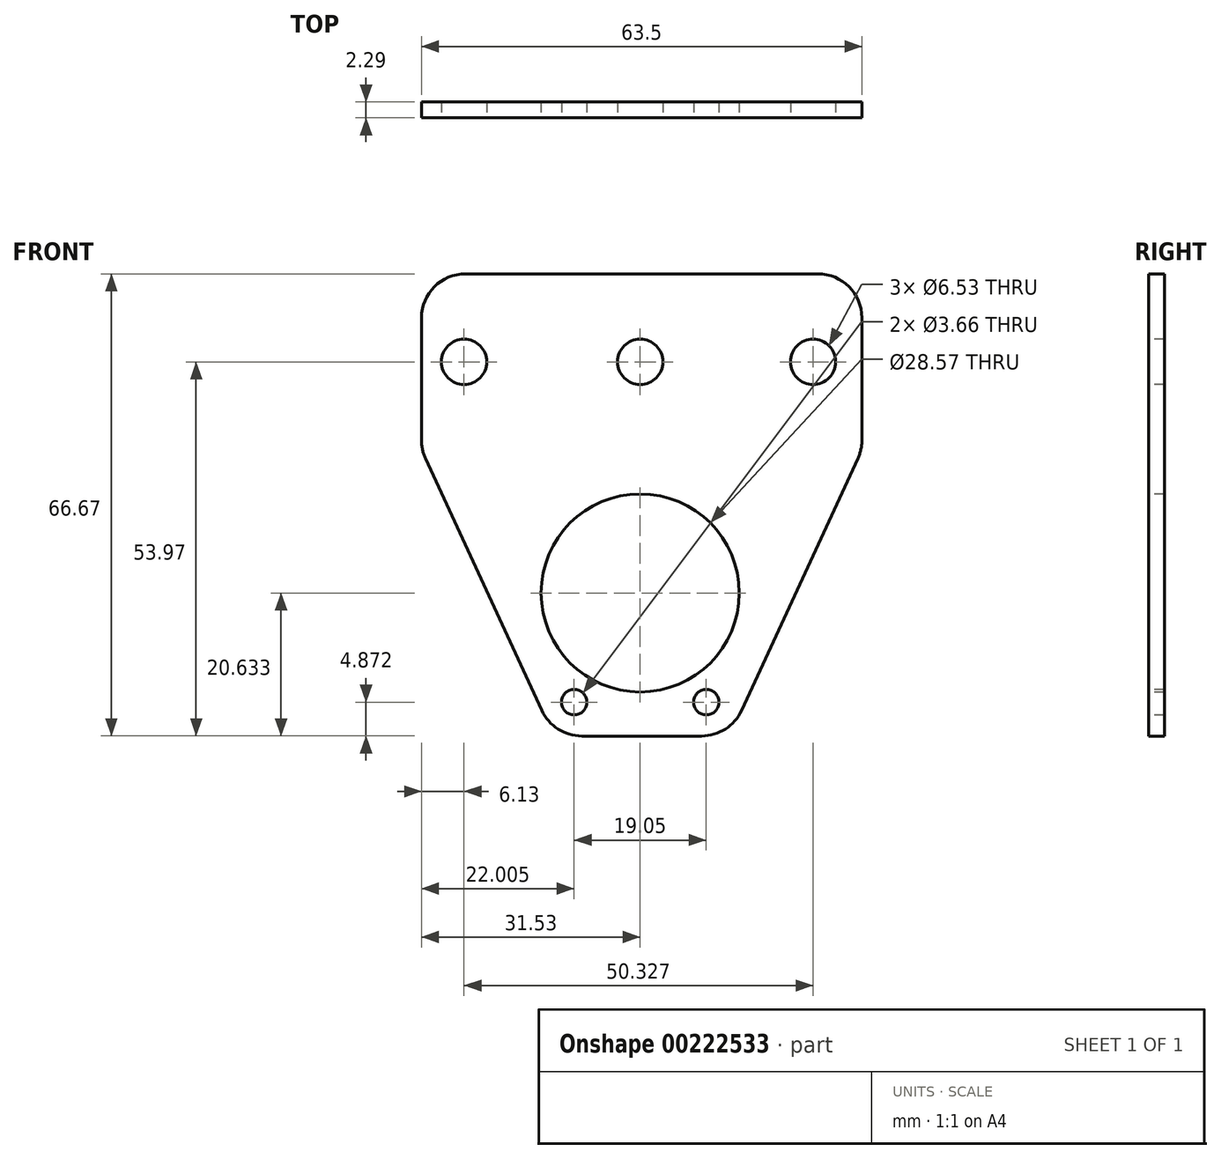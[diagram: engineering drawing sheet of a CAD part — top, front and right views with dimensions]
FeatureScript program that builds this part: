
annotation { "Feature Type Name" : "Feature", "Feature Type Description" : "" }
export const myFeature = defineFeature(function(context is Context, id is Id, definition is map)
    precondition{}
    {
        {
            var Q0;
            Q0=qCreatedBy(makeId("Front.planeOp"),FACE);
            var sketch = newSketch(context, id + "F0", { "sketchPlane" : qUnion([Q0])});
            skLineSegment(sketch, "E0", {"start": v(-25.18, 42.8) * mm, "end": v(25.62, 42.8) * mm});
            skLineSegment(sketch, "E1", {"start": v(31.97, 36.44) * mm, "end": v(31.97, 18.78) * mm});
            skLineSegment(sketch, "E2", {"start": v(31.38, 16.12) * mm, "end": v(14.62, -20.2) * mm});
            skLineSegment(sketch, "E3", {"start": v(8.85, -23.88) * mm, "end": v(-8.42, -23.88) * mm});
            skLineSegment(sketch, "E4", {"start": v(-14.19, -20.2) * mm, "end": v(-30.95, 16.12) * mm});
            skLineSegment(sketch, "E5", {"start": v(-31.53, 18.78) * mm, "end": v(-31.53, 36.44) * mm});
            skPoint(sketch, "E6.visualSharp", {"position": v(-31.53, 42.8) * mm});
            skArc(sketch, "E6.filletArc", {"start": v(-25.18, 42.8) * mm, "mid": v(-29.67, 40.93) * mm, "end": v(-31.53, 36.44) * mm});
            skPoint(sketch, "E7.visualSharp", {"position": v(31.97, 42.8) * mm});
            skArc(sketch, "E7.filletArc", {"start": v(31.97, 36.44) * mm, "mid": v(30.1, 40.93) * mm, "end": v(25.62, 42.8) * mm});
            skPoint(sketch, "E8.visualSharp", {"position": v(31.97, 17.4) * mm});
            skArc(sketch, "E8.filletArc", {"start": v(31.38, 16.12) * mm, "mid": v(31.82, 17.42) * mm, "end": v(31.97, 18.78) * mm});
            skPoint(sketch, "E9.visualSharp", {"position": v(-31.53, 17.4) * mm});
            skArc(sketch, "E9.filletArc", {"start": v(-31.53, 18.78) * mm, "mid": v(-31.39, 17.42) * mm, "end": v(-30.95, 16.12) * mm});
            skPoint(sketch, "E10.visualSharp", {"position": v(-12.48, -23.88) * mm});
            skArc(sketch, "E10.filletArc", {"start": v(-14.19, -20.2) * mm, "mid": v(-11.84, -22.88) * mm, "end": v(-8.42, -23.88) * mm});
            skPoint(sketch, "E11.visualSharp", {"position": v(12.92, -23.88) * mm});
            skArc(sketch, "E11.filletArc", {"start": v(8.85, -23.88) * mm, "mid": v(12.28, -22.88) * mm, "end": v(14.62, -20.2) * mm});
            skSolve(sketch);
        }
        {
            var Q0;
            Q0=makeQuery(id+"F0.imprint","IMPRINT",FACE,{"disambiguationData":[TD([[makeQuery(id+"F0.imprint","IMPRINT",EDGE,{"derivedFrom":sQuery(id+"F0.wireOp",EDGE,"E0")}),-1.0]])]});
            extrude(context, id + "F1", {"entities" : qUnion([Q0]), "depth" : 2.3 * mm});
        }
        {
            var Q0;
            Q0=makeQuery(id+"F1.opExtrude","CAP_FACE",FACE,{"disambiguationData":[OSD([sQuery(id+"F0.wireOp",EDGE,"E0"),sQuery(id+"F0.wireOp",EDGE,"E1"),sQuery(id+"F0.wireOp",EDGE,"E2"),sQuery(id+"F0.wireOp",EDGE,"E3"),sQuery(id+"F0.wireOp",EDGE,"E4"),sQuery(id+"F0.wireOp",EDGE,"E5"),sQuery(id+"F0.wireOp",EDGE,"E6.filletArc"),sQuery(id+"F0.wireOp",EDGE,"E7.filletArc"),sQuery(id+"F0.wireOp",EDGE,"E8.filletArc"),sQuery(id+"F0.wireOp",EDGE,"E9.filletArc"),sQuery(id+"F0.wireOp",EDGE,"E10.filletArc"),sQuery(id+"F0.wireOp",EDGE,"E11.filletArc")])],"isStart":false});
            var sketch = newSketch(context, id + "F2", { "sketchPlane" : qUnion([Q0])});
            skPoint(sketch, "E12", {"position": v(-25.4, 30.1) * mm});
            skPoint(sketch, "E13", {"position": v(0, 30.1) * mm});
            skPoint(sketch, "E14", {"position": v(24.93, 30.1) * mm});
            skSolve(sketch);
        }
        {
            var Q0;
            Q0=sQuery(id+"F2.wireOp",VERTEX,"E12");
            var Q1;
            Q1=sQuery(id+"F2.wireOp",VERTEX,"E13");
            var Q2;
            Q2=sQuery(id+"F2.wireOp",VERTEX,"E14");
            var Q3;
            Q3=makeQuery(id+"F1.opExtrude","SWEPT_BODY",BODY,{"disambiguationData":[OSD([sQuery(id+"F0.wireOp",EDGE,"E0"),sQuery(id+"F0.wireOp",EDGE,"E1"),sQuery(id+"F0.wireOp",EDGE,"E2"),sQuery(id+"F0.wireOp",EDGE,"E3"),sQuery(id+"F0.wireOp",EDGE,"E4"),sQuery(id+"F0.wireOp",EDGE,"E5"),sQuery(id+"F0.wireOp",EDGE,"E6.filletArc"),sQuery(id+"F0.wireOp",EDGE,"E7.filletArc"),sQuery(id+"F0.wireOp",EDGE,"E8.filletArc"),sQuery(id+"F0.wireOp",EDGE,"E9.filletArc"),sQuery(id+"F0.wireOp",EDGE,"E10.filletArc"),sQuery(id+"F0.wireOp",EDGE,"E11.filletArc")])]});
            hole(context, id + "F3", {"style" : HoleStyle.SIMPLE, "endStyle" : HoleEndStyle.THROUGH, "standardTappedOrClearance" : lookupTablePath({ "standard" : "ANSI", "fit" : "Close", "size" : "1/4", "type" : "Clearance" }), "standardBlindInLast" : lookupTablePath({ "fit" : "Close", "standard" : "ANSI", "size" : "1/4", "type" : "Clearance" }), "holeDiameter" : 6.53 * mm, "locations" : qUnion([Q0, Q1, Q2]), "scope" : qUnion([Q3]), "isTappedThrough" : true});
        }
        {
            var Q0;
            Q0=makeQuery(id+"F1.opExtrude","CAP_FACE",FACE,{"disambiguationData":[OSD([sQuery(id+"F0.wireOp",EDGE,"E0"),sQuery(id+"F0.wireOp",EDGE,"E1"),sQuery(id+"F0.wireOp",EDGE,"E2"),sQuery(id+"F0.wireOp",EDGE,"E3"),sQuery(id+"F0.wireOp",EDGE,"E4"),sQuery(id+"F0.wireOp",EDGE,"E5"),sQuery(id+"F0.wireOp",EDGE,"E6.filletArc"),sQuery(id+"F0.wireOp",EDGE,"E7.filletArc"),sQuery(id+"F0.wireOp",EDGE,"E8.filletArc"),sQuery(id+"F0.wireOp",EDGE,"E9.filletArc"),sQuery(id+"F0.wireOp",EDGE,"E10.filletArc"),sQuery(id+"F0.wireOp",EDGE,"E11.filletArc")])],"isStart":false});
            var sketch = newSketch(context, id + "F4", { "sketchPlane" : qUnion([Q0])});
            skPoint(sketch, "E15", {"position": v(0, -3.25) * mm});
            skSolve(sketch);
        }
        {
            var Q0;
            Q0=sQuery(id+"F4.wireOp",VERTEX,"E15");
            var Q1;
            Q1=makeQuery(id+"F1.opExtrude","SWEPT_BODY",BODY,{"disambiguationData":[OSD([sQuery(id+"F0.wireOp",EDGE,"E0"),sQuery(id+"F0.wireOp",EDGE,"E1"),sQuery(id+"F0.wireOp",EDGE,"E2"),sQuery(id+"F0.wireOp",EDGE,"E3"),sQuery(id+"F0.wireOp",EDGE,"E4"),sQuery(id+"F0.wireOp",EDGE,"E5"),sQuery(id+"F0.wireOp",EDGE,"E6.filletArc"),sQuery(id+"F0.wireOp",EDGE,"E7.filletArc"),sQuery(id+"F0.wireOp",EDGE,"E8.filletArc"),sQuery(id+"F0.wireOp",EDGE,"E9.filletArc"),sQuery(id+"F0.wireOp",EDGE,"E10.filletArc"),sQuery(id+"F0.wireOp",EDGE,"E11.filletArc")])]});
            hole(context, id + "F5", {"style" : HoleStyle.SIMPLE, "endStyle" : HoleEndStyle.THROUGH, "holeDiameter" : 28.57 * mm, "locations" : qUnion([Q0]), "scope" : qUnion([Q1]), "isTappedThrough" : true});
        }
        {
            var Q0;
            Q0=makeQuery(id+"F1.opExtrude","CAP_FACE",FACE,{"disambiguationData":[OSD([sQuery(id+"F0.wireOp",EDGE,"E0"),sQuery(id+"F0.wireOp",EDGE,"E1"),sQuery(id+"F0.wireOp",EDGE,"E2"),sQuery(id+"F0.wireOp",EDGE,"E3"),sQuery(id+"F0.wireOp",EDGE,"E4"),sQuery(id+"F0.wireOp",EDGE,"E5"),sQuery(id+"F0.wireOp",EDGE,"E6.filletArc"),sQuery(id+"F0.wireOp",EDGE,"E7.filletArc"),sQuery(id+"F0.wireOp",EDGE,"E8.filletArc"),sQuery(id+"F0.wireOp",EDGE,"E9.filletArc"),sQuery(id+"F0.wireOp",EDGE,"E10.filletArc"),sQuery(id+"F0.wireOp",EDGE,"E11.filletArc")])],"isStart":false});
            var sketch = newSketch(context, id + "F6", { "sketchPlane" : qUnion([Q0])});
            skPoint(sketch, "E16", {"position": v(-9.52, -19) * mm});
            skPoint(sketch, "E17", {"position": v(9.53, -19) * mm});
            skSolve(sketch);
        }
        {
            var Q0;
            Q0=sQuery(id+"F6.wireOp",VERTEX,"E16");
            var Q1;
            Q1=sQuery(id+"F6.wireOp",VERTEX,"E17");
            var Q2;
            Q2=makeQuery(id+"F1.opExtrude","SWEPT_BODY",BODY,{"disambiguationData":[OSD([sQuery(id+"F0.wireOp",EDGE,"E0"),sQuery(id+"F0.wireOp",EDGE,"E1"),sQuery(id+"F0.wireOp",EDGE,"E2"),sQuery(id+"F0.wireOp",EDGE,"E3"),sQuery(id+"F0.wireOp",EDGE,"E4"),sQuery(id+"F0.wireOp",EDGE,"E5"),sQuery(id+"F0.wireOp",EDGE,"E6.filletArc"),sQuery(id+"F0.wireOp",EDGE,"E7.filletArc"),sQuery(id+"F0.wireOp",EDGE,"E8.filletArc"),sQuery(id+"F0.wireOp",EDGE,"E9.filletArc"),sQuery(id+"F0.wireOp",EDGE,"E10.filletArc"),sQuery(id+"F0.wireOp",EDGE,"E11.filletArc")])]});
            hole(context, id + "F7", {"style" : HoleStyle.SIMPLE, "endStyle" : HoleEndStyle.THROUGH, "standardTappedOrClearance" : lookupTablePath({ "standard" : "ANSI", "fit" : "Close", "size" : "#6", "type" : "Clearance" }), "standardBlindInLast" : lookupTablePath({ "fit" : "Close", "standard" : "ANSI", "size" : "#6", "type" : "Clearance" }), "holeDiameter" : 3.66 * mm, "locations" : qUnion([Q0, Q1]), "scope" : qUnion([Q2]), "isTappedThrough" : true});
        }
    });
